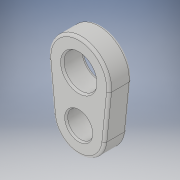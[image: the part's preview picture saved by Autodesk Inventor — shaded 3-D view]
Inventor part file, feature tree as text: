
AUTODESK INVENTOR PART (.ipt)
format: ipt  version: 2018.3 (Build 223284000, 284)  size: 172,032 bytes
history: native  units: in
note: dims shown in document units (in); Inventor stores cm internally (conversion verified against a paired STEP export)
features: hole x4, extrude x1, fillet x1, sketch x1
ambient origin geometry x8: Origin, YZ Plane, XZ Plane, XY Plane, X Axis, Y Axis, Z Axis, Center Point
bodies: Solid1 (feature_tree)
feature tree (7):
  extrude  "Extrusion1"  Depth=0.015in
  hole  "Hole1"  [1 undecoded]
  hole  "Hole2"  [1 undecoded]
  hole  "Hole3"  [1 undecoded]
  hole  "Hole4"  [1 undecoded]
  fillet  "Fillet1"  Radius=1.0in
  sketch  "Sketch1"  dims[d0=0.2045in d1=0.1565in d2=0.278in d3=0.368in d4=0.312in d5=0.136in d6=0.0in d7=1.0in d8=1.0in d9=0.2045in d10=0.75in d11=0.22in d12=0.25in d13=60.0deg d14=1.0in d15=0.8108in d16=1.0in d17=1.0in d18=0.2045in d19=0.75in d20=0.22in d21=0.25in d22=60.0deg d23=1.0in d24=0.8108in d25=1.0in d26=1.0in d27=0.1565in d28=0.75in d29=0.17in d30=0.25in d31=60.0deg d32=1.0in d33=0.8108in d34=1.0in d35=1.0in d36=0.1565in d37=0.75in d38=0.17in d39=0.25in d40=60.0deg d41=1.0in d42=0.8108in d43=0.015in]
note: 4 required parameter values undecoded (feature->parameter linkage not recoverable at this tier; creation-order binding heuristic only, values carry confidence <= 0.55)
